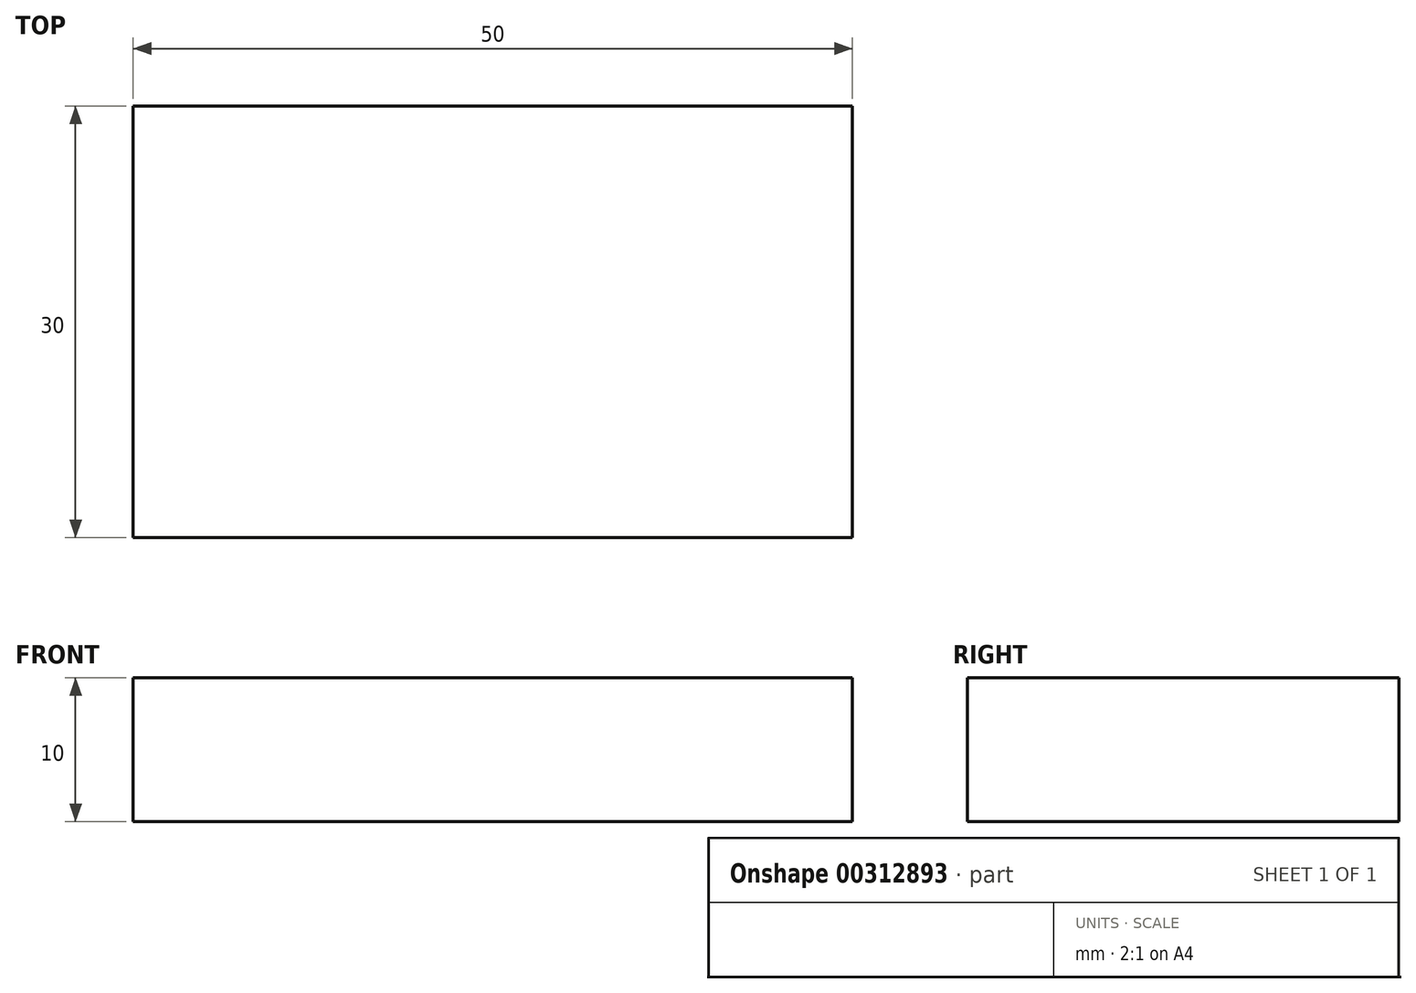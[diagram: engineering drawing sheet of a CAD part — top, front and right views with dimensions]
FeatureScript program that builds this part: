
annotation { "Feature Type Name" : "Feature", "Feature Type Description" : "" }
export const myFeature = defineFeature(function(context is Context, id is Id, definition is map)
    precondition{}
    {
        {
            var Q0;
            Q0=qCreatedBy(makeId("Top.planeOp"),FACE);
            var sketch = newSketch(context, id + "F0", { "sketchPlane" : qUnion([Q0])});
            skLineSegment(sketch, "E0.bottom", {"start": v(0, 0) * mm, "end": v(50, 0) * mm});
            skLineSegment(sketch, "E0.top", {"start": v(0, 30) * mm, "end": v(50, 30) * mm});
            skLineSegment(sketch, "E0.left", {"start": v(0, 0) * mm, "end": v(0, 30) * mm});
            skLineSegment(sketch, "E0.right", {"start": v(50, 0) * mm, "end": v(50, 30) * mm});
            skSolve(sketch);
        }
        {
            var Q0;
            Q0 = qSketchRegion(id + "F0", true);
            extrude(context, id + "F1", {"entities" : qUnion([Q0]), "depth" : 10 * mm, "offsetDistance" : 25 * mm});
        }
    });
